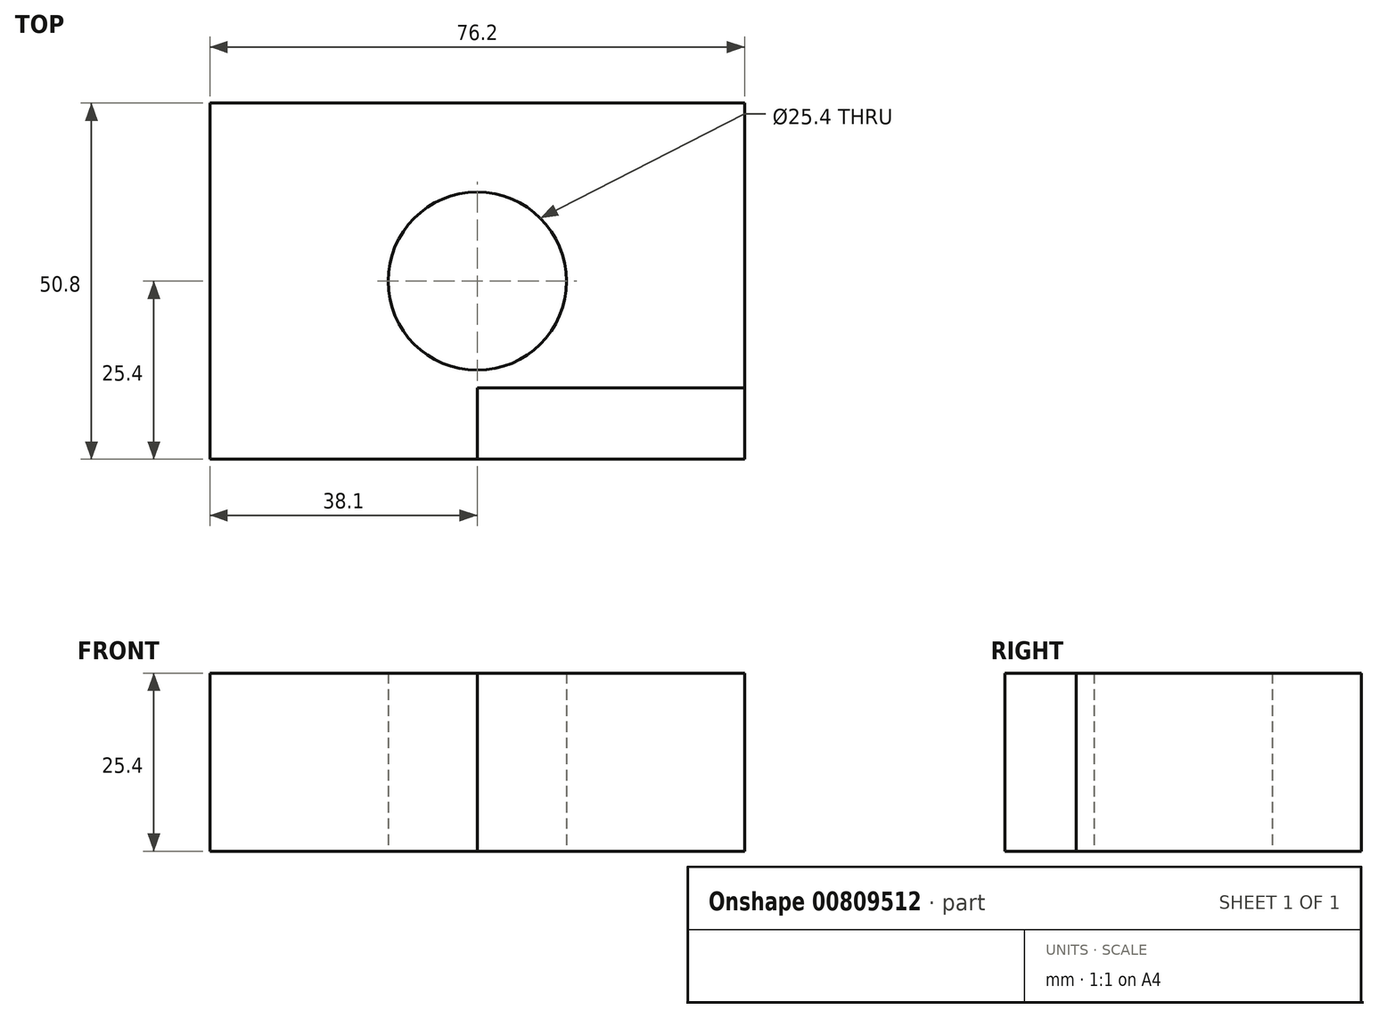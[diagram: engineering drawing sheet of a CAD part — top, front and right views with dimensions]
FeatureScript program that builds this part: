
annotation { "Feature Type Name" : "Feature", "Feature Type Description" : "" }
export const myFeature = defineFeature(function(context is Context, id is Id, definition is map)
    precondition{}
    {
        {
            var Q0;
            Q0=qCreatedBy(makeId("Top.planeOp"),FACE);
            var sketch = newSketch(context, id + "F0", { "sketchPlane" : qUnion([Q0])});
            skLineSegment(sketch, "E0.bottom", {"start": v(0, -36.62) * mm, "end": v(0, -36.62) * mm});
            skLineSegment(sketch, "E0.top", {"start": v(0, 36.62) * mm, "end": v(0, 36.62) * mm});
            skLineSegment(sketch, "E0.left", {"start": v(0, -36.62) * mm, "end": v(0, 36.62) * mm});
            skLineSegment(sketch, "E0.right", {"start": v(0, -36.62) * mm, "end": v(0, 36.62) * mm});
            skPoint(sketch, "E0.middle", {"position": v(0, 0) * mm});
            skLineSegment(sketch, "E1.bottom", {"start": v(-38.1, 25.4) * mm, "end": v(38.1, 25.4) * mm});
            skLineSegment(sketch, "E1.top", {"start": v(-38.1, -25.4) * mm, "end": v(38.1, -25.4) * mm});
            skLineSegment(sketch, "E1.left", {"start": v(-38.1, 25.4) * mm, "end": v(-38.1, -25.4) * mm});
            skLineSegment(sketch, "E1.right", {"start": v(38.1, 25.4) * mm, "end": v(38.1, -25.4) * mm});
            skCircle(sketch, "E2", {"center": v(0, 0) * mm, "radius": 12.7 * mm});
            skSolve(sketch);
        }
        {
            var Q0;
            {var subQ5=sQuery(id+"F0.wireOp",EDGE,"E1.right");Q0=makeQuery(id+"F0.imprint","IMPRINT",FACE,{"disambiguationData":[TD([[makeQuery(id+"F0.imprint","IMPRINT",EDGE,{"derivedFrom":subQ5}),-1.0]])]});}
            var sketch = newSketch(context, id + "F1", { "sketchPlane" : qUnion([Q0])});
            skLineSegment(sketch, "E3.bottom", {"start": v(-55.8, -15.23) * mm, "end": v(55.8, -15.23) * mm});
            skLineSegment(sketch, "E3.top", {"start": v(-55.8, 15.23) * mm, "end": v(55.8, 15.23) * mm});
            skLineSegment(sketch, "E3.left", {"start": v(-55.8, -15.23) * mm, "end": v(-55.8, 15.23) * mm});
            skLineSegment(sketch, "E3.right", {"start": v(55.8, -15.23) * mm, "end": v(55.8, 15.23) * mm});
            skPoint(sketch, "E3.middle", {"position": v(0, 0) * mm});
            skSolve(sketch);
        }
        {
            var Q0;
            {var subQ1=sQuery(id+"F0.wireOp",EDGE,"E1.top");var subQ6=sQuery(id+"F0.wireOp",EDGE,"E1.right");var subQ9=makeQuery(id+"F0.imprint","IMPRINT",EDGE,{"disambiguationData":[TD([[makeQuery(id+"F0.imprint","INTERSECT",VERTEX,{"derivedFrom":[subQ1,subQ6]}),1.0]])],"derivedFrom":subQ1});Q0=makeQuery(id+"F1.imprint","IMPRINT",FACE,{"disambiguationData":[TD([[makeQuery(id+"F1.imprint","IMPRINT",EDGE,{"derivedFrom":subQ9}),1.0]])]});}
            var Q1;
            {var subQ0=sQuery(id+"F0.wireOp",EDGE,"E1.left");Q1=makeQuery(id+"F0.imprint","IMPRINT",FACE,{"disambiguationData":[TD([[makeQuery(id+"F0.imprint","IMPRINT",EDGE,{"derivedFrom":subQ0}),1.0]])]});}
            var Q2;
            {var subQ0=sQuery(id+"F0.wireOp",EDGE,"E1.right");Q2=makeQuery(id+"F0.imprint","IMPRINT",FACE,{"disambiguationData":[TD([[makeQuery(id+"F0.imprint","IMPRINT",EDGE,{"derivedFrom":subQ0}),-1.0]])]});}
            var Q3;
            {var subQ0=sQuery(id+"F0.wireOp",EDGE,"E2");var subQ1=sQuery(id+"F0.wireOp",EDGE,"E0.right");var subQ2=makeQuery(id+"F0.imprint","INTERSECT",VERTEX,{"disambiguationData":[OD(0.0)],"derivedFrom":[subQ1,subQ0]});Q3=makeQuery(id+"F0.imprint","IMPRINT",FACE,{"disambiguationData":[TD([[makeQuery(id+"F0.imprint","IMPRINT",EDGE,{"disambiguationData":[TD([[subQ2,-1.0]])],"derivedFrom":subQ1}),-1.0]])]});}
            extrude(context, id + "F2", {"entities" : qUnion([Q0, Q1, Q2, Q3]), "depth" : 25.4 * mm, "offsetDistance" : 25.4 * mm});
        }
    });
